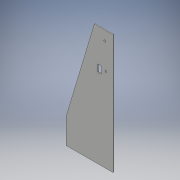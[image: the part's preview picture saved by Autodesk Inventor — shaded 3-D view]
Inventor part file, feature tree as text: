
AUTODESK INVENTOR PART (.ipt)
format: ipt  version: 2018 (Build 220112000, 112)  size: 135,168 bytes
history: native  units: mm
features: extrude x2, sketch x2, other x1, fillet x1
ambient origin geometry x8: Origin, YZ Plane, XZ Plane, XY Plane, X Axis, Y Axis, Z Axis, Center Point
bodies: Body1 (feature_tree)
feature tree (6):
  other  "ソリッド1"
  extrude  "押し出し1"  Depth=509.0mm
  extrude  "押し出し2"  Depth=200.0mm
  fillet  "フィレット1"  Radius=109.0mm
  sketch  "スケッチ1"
  sketch  "スケッチ2"
